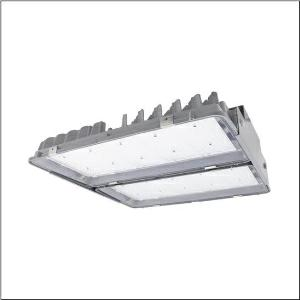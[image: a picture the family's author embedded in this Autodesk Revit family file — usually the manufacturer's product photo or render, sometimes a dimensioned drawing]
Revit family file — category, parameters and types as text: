
# Revit family: highbay_11xtreme_51hf82db4vma
name_source: partatom
category: Lighting Fixtures
units: mm (PartAtom-declared; Revit-internal decimal feet)

## family parameters
Cut with Voids When Loaded = No
Host = Face
Light Source = No
Part Type = Normal
Room Calculation Point = No
Round Connector Dimension = Use Diameter
Shared = No

## types (1)
- --- (1 x LED, 68500 lm, 380.3 W, 4000K)
    Apparent Load = 380 VA
    CIE Flux Codes = 84 96 100 100 100
    Color Rendering = 80
    Color Temperature = 4000K
    Default Elevation = 1800 mm
    Description = Highbay 11Xtreme, LED high bay luminaire, primary light control with lens, of PMMA, primary optical cover: cover, of toughened safety glass, light emission: direct distribution, primary light characteristic: symmetric, installation type: suspended mounting, surface-mounted, 2x LED module,for 1x 2x LED, rated luminous flux: 68.500lm, luminous efficacy: 180lm/W, light colour: 840, colour temperature: 4000K, with cable H07RN-F 5x 1.5mm², mains connection: 220..240V, AC, 50/60Hz, cable length: 1,5m, rated input power: 380W, luminaire housing, of diecast aluminium, partly coated, silver, length: 595mm, width: 560mm, height: 195mm, protection rating (complete): IP66, insulation class (complete): insulation class I (protective earthing), certification: CE, ENEC, UKCA, protection symbol: D, ball protection: ball impact resistant according to DIN VDE 0710 part 13 (with chain suspension), impact resistance: IK08, permissible operating ambient temperature: -25..+45°C, reducing of maximum allowable ambient temperature of 5°C with ceiling mounting, packaging unit: 1 piece
    Height = 157 mm
    Lamp = 1 x LED
    Lamp Light Flux = 68500 lm
    Lamp Power = 380.3 W
    Lamp count = 1
    Length = 593 mm
    Luminous efficacy = 180 lm/W
    Manufacturer = Siteco
    ModVariant = No
    Model = 51HF82DB4VMA
    Mounting Place = Ceiling
    Mounting Type = Pendant
    Number of Poles = 1
    OnlyDefault = Yes
    Power Factor = 1
    Product Name = Highbay 11Xtreme
    Product group = LED high bay luminaire
    ProductGroupID = 903
    Protection Class = Protection class I
    Protection Degree = IP 66
    RLX_Detail_Level = 1
    RLX_Emergency_Light_Flux = 0 lm
    RLX_Emergency_Type = 0
    RLX_Emergency_Type_DB = No
    RlxData = <blob elided: 34345 chars, md5=74e01785>
    Socket = socket
    Standby Power = 0 W
    System Light Flux = 68500 lm
    System Power = 380 W
    Type Comments = factory setting: luminous flux: 100 % | dim-lin: 254 | 1257 mA
    Type Image = l_1258340.jpg
    URL = http://relux.com
    VarID = @adj_035461
    Voltage = 0 V
    Weight = 0.00 kg
    Width = 568 mm

## geometry (parser evidence)
native form markers: Blend x4, Sweep x11
no freeform markers — native parametric forms only
